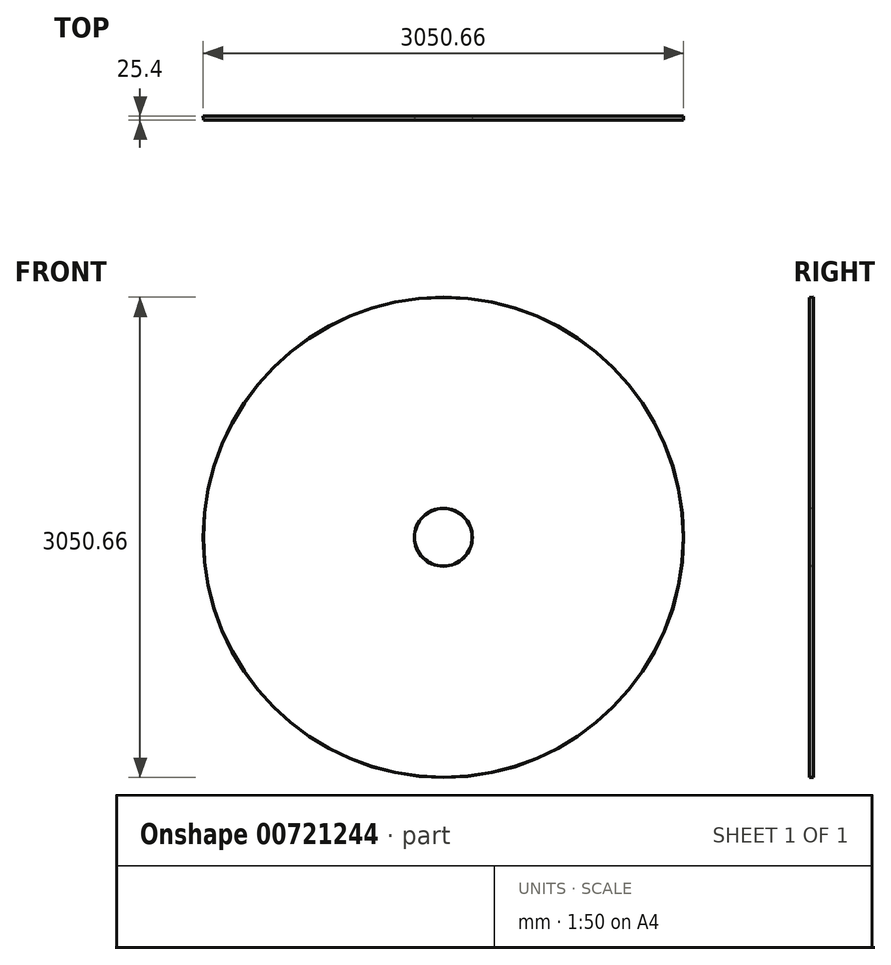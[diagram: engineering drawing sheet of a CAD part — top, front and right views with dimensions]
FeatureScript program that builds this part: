
annotation { "Feature Type Name" : "Feature", "Feature Type Description" : "" }
export const myFeature = defineFeature(function(context is Context, id is Id, definition is map)
    precondition{}
    {
        {
            var Q0;
            Q0=qCreatedBy(makeId("Front.planeOp"),FACE);
            var sketch = newSketch(context, id + "F0", { "sketchPlane" : qUnion([Q0])});
            skCircle(sketch, "E0", {"center": v(0, 0) * mm, "radius": 1524 * mm});
            skCircle(sketch, "E1", {"center": v(0, 0) * mm, "radius": 184.15 * mm});
            skSolve(sketch);
        }
        {
            var Q0;
            Q0=makeQuery(id+"F0.imprint","IMPRINT",FACE,{"disambiguationData":[TD([[makeQuery(id+"F0.imprint","IMPRINT",EDGE,{"derivedFrom":sQuery(id+"F0.wireOp",EDGE,"E0")}),1.0]])]});
            extrude(context, id + "F1", {"entities" : qUnion([Q0]), "oppositeDirection" : true, "depth" : 25.4 * mm, "offsetDistance" : 25.4 * mm, "hasDraft" : true, "draftAngle" : 3 * degree});
        }
    });
